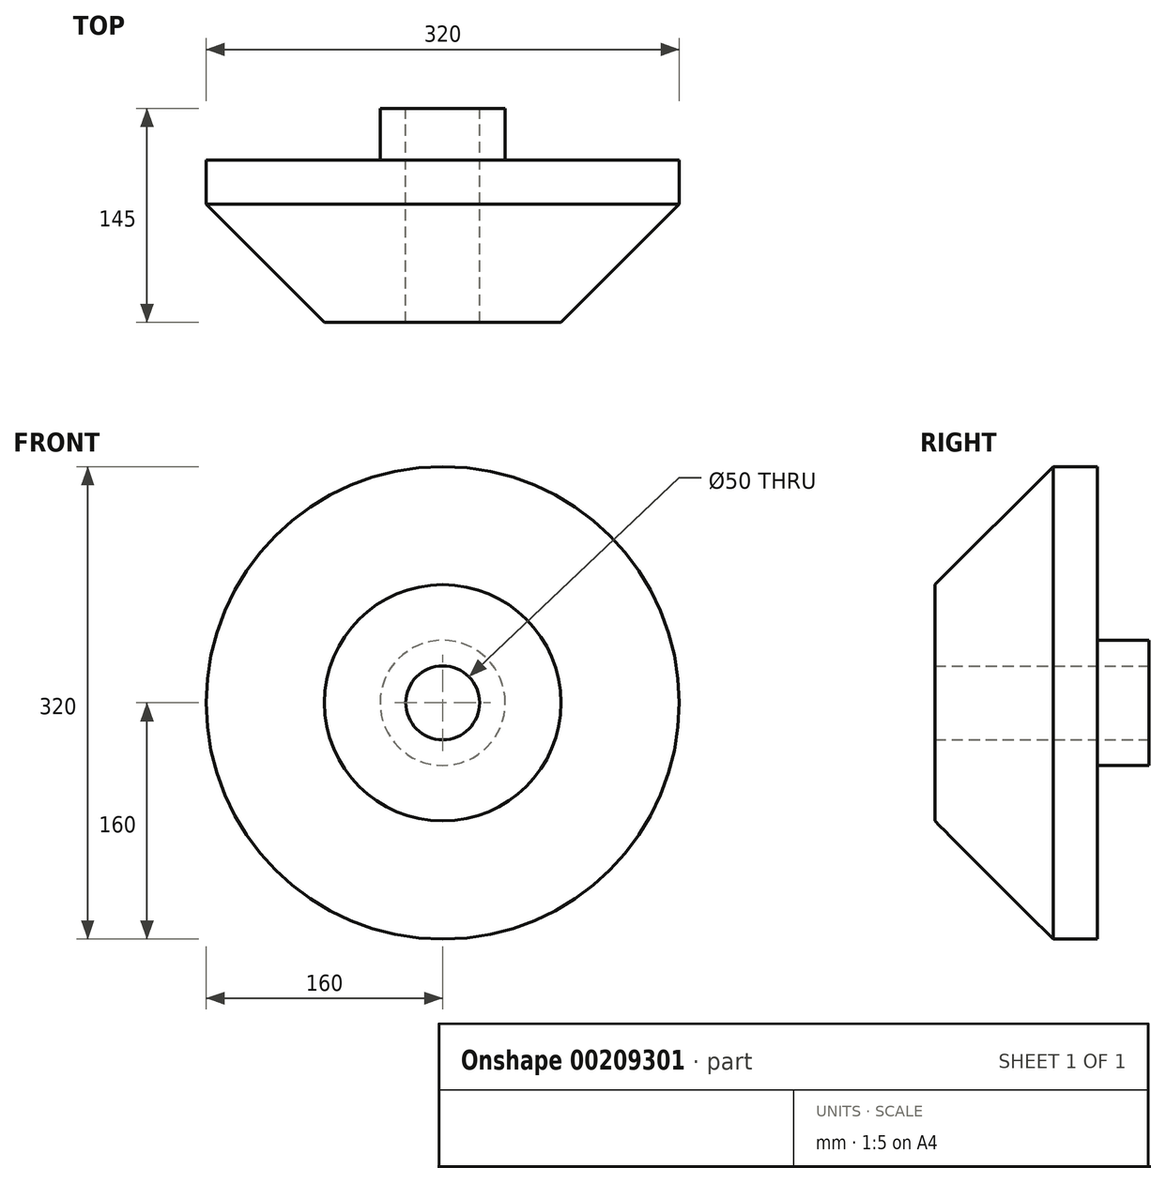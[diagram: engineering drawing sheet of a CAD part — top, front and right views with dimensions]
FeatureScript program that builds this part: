
annotation { "Feature Type Name" : "Feature", "Feature Type Description" : "" }
export const myFeature = defineFeature(function(context is Context, id is Id, definition is map)
    precondition{}
    {
        {
            var Q0;
            Q0=qCreatedBy(makeId("Front.planeOp"),FACE);
            var sketch = newSketch(context, id + "F0", { "sketchPlane" : qUnion([Q0])});
            skCircle(sketch, "E0", {"center": v(0, 0) * mm, "radius": 25 * mm});
            skCircle(sketch, "E1", {"center": v(0, 0) * mm, "radius": 42.35 * mm});
            skCircle(sketch, "E2", {"center": v(0, 0) * mm, "radius": 160 * mm});
            skSolve(sketch);
        }
        {
            var Q0;
            Q0=makeQuery(id+"F0.imprint","IMPRINT",FACE,{"disambiguationData":[TD([[makeQuery(id+"F0.imprint","IMPRINT",EDGE,{"derivedFrom":sQuery(id+"F0.wireOp",EDGE,"E1")}),-1.0]])]});
            var Q1;
            Q1=makeQuery(id+"F0.imprint","IMPRINT",FACE,{"disambiguationData":[TD([[makeQuery(id+"F0.imprint","IMPRINT",EDGE,{"derivedFrom":sQuery(id+"F0.wireOp",EDGE,"E0")}),-1.0]])]});
            extrude(context, id + "F1", {"entities" : qUnion([Q0, Q1]), "depth" : 110 * mm});
        }
        {
            var Q0;
            Q0=makeQuery(id+"F0.imprint","IMPRINT",FACE,{"disambiguationData":[TD([[makeQuery(id+"F0.imprint","IMPRINT",EDGE,{"derivedFrom":sQuery(id+"F0.wireOp",EDGE,"E0")}),-1.0]])]});
            extrude(context, id + "F2", {"entities" : qUnion([Q0]), "operationType" : NewBodyOperationType.ADD, "oppositeDirection" : true, "depth" : 35 * mm});
        }
        {
            var Q0;
            Q0=makeQuery(id+"F1.opExtrude","CAP_EDGE",EDGE,{"disambiguationData":[OSD([sQuery(id+"F0.wireOp",EDGE,"E2")])],"isStart":false});
            chamfer(context, id + "F3", {"entities" : qUnion([Q0]), "width" : 80 * mm, "tangentPropagation" : true});
        }
    });
